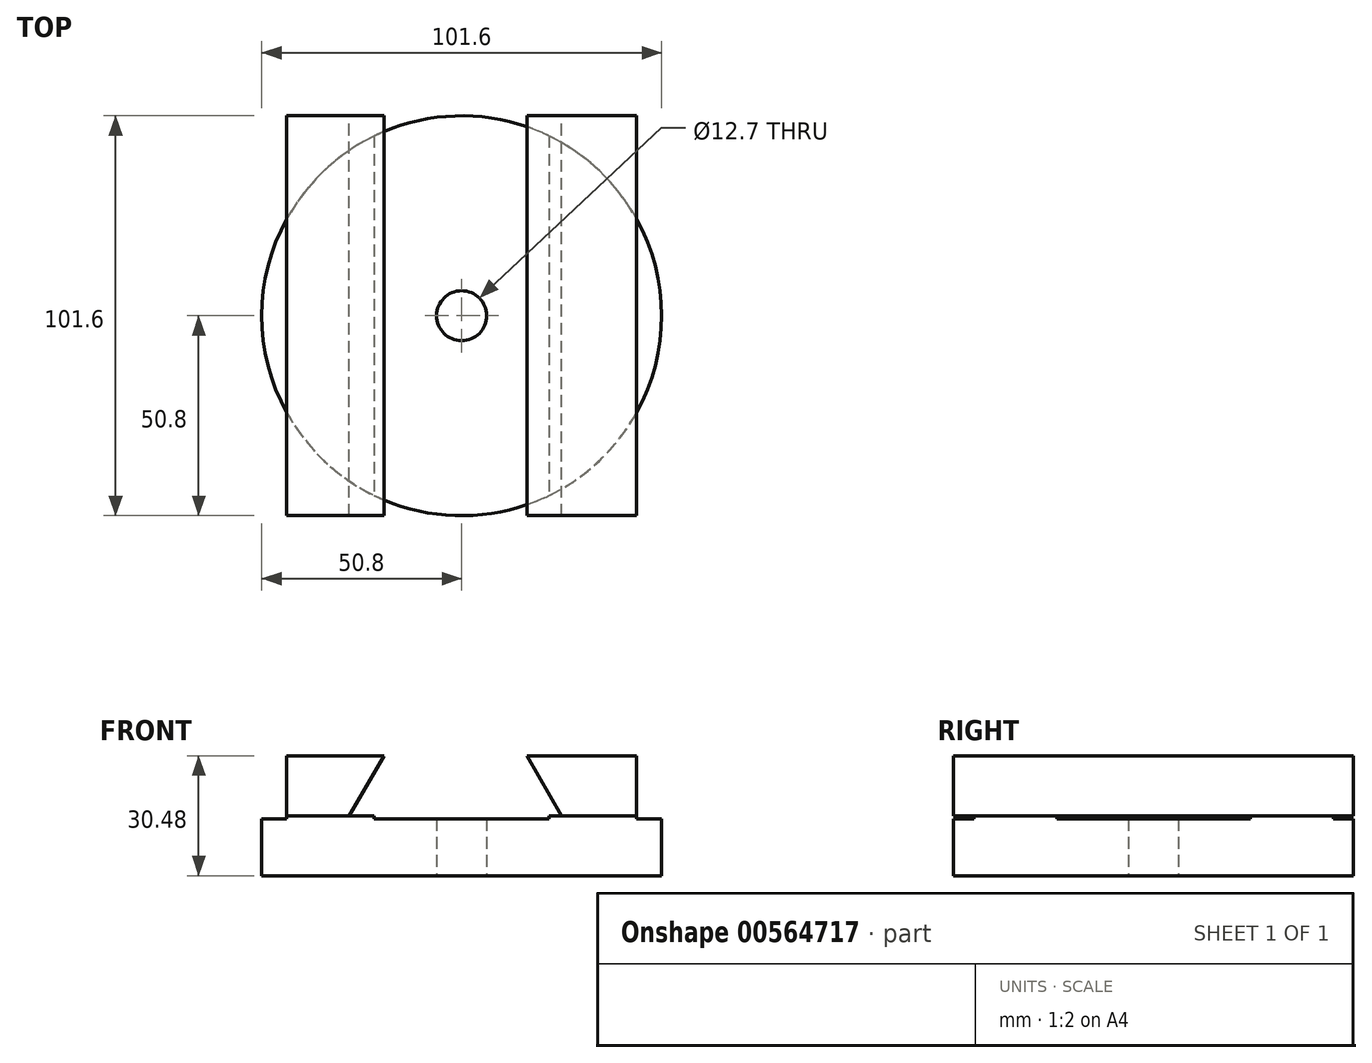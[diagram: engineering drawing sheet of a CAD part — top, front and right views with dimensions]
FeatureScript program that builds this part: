
annotation { "Feature Type Name" : "Feature", "Feature Type Description" : "" }
export const myFeature = defineFeature(function(context is Context, id is Id, definition is map)
    precondition{}
    {
        {
            var Q0;
            Q0=qCreatedBy(makeId("Top.planeOp"),FACE);
            var sketch = newSketch(context, id + "F0", { "sketchPlane" : qUnion([Q0])});
            skCircle(sketch, "E0", {"center": v(0, 0) * mm, "radius": 50.8 * mm});
            skSolve(sketch);
        }
        {
            var Q0;
            Q0=makeQuery(id+"F0.imprint","IMPRINT",FACE,{"disambiguationData":[TD([[makeQuery(id+"F0.imprint","IMPRINT",EDGE,{"derivedFrom":sQuery(id+"F0.wireOp",EDGE,"E0")}),1.0]])]});
            extrude(context, id + "F1", {"entities" : qUnion([Q0]), "depth" : 15.24 * mm, "offsetDistance" : 25.4 * mm});
        }
        {
            var Q0;
            Q0=sQuery(id+"F0.wireOp",VERTEX,"E0.center");
            var Q1;
            Q1=makeQuery(id+"F1.opExtrude","SWEPT_BODY",BODY,{"disambiguationData":[OSD([sQuery(id+"F0.wireOp",EDGE,"E0")])]});
            hole(context, id + "F2", {"style" : HoleStyle.SIMPLE, "endStyle" : HoleEndStyle.THROUGH, "oppositeDirection" : true, "holeDiameter" : 12.7 * mm, "isTappedThrough" : true, "tappedDepth" : 12.7 * mm, "tapClearance" : 3, "locations" : qUnion([Q0]), "scope" : qUnion([Q1])});
        }
        {
            var Q0;
            Q0=makeQuery(id+"F1.opExtrude","CAP_FACE",FACE,{"disambiguationData":[OSD([sQuery(id+"F0.wireOp",EDGE,"E0")])],"isStart":false});
            var sketch = newSketch(context, id + "F3", { "sketchPlane" : qUnion([Q0])});
            skLineSegment(sketch, "E1", {"start": v(-25.4, 44) * mm, "end": v(-25.4, -44) * mm});
            skLineSegment(sketch, "E2", {"start": v(25.4, 44) * mm, "end": v(25.4, -44) * mm});
            skLineSegment(sketch, "E3", {"start": v(0, 50.8) * mm, "end": v(0, -50.8) * mm, "construction": true});
            skLineSegment(sketch, "E4", {"start": v(-44.45, 24.6) * mm, "end": v(-44.45, -24.6) * mm});
            skLineSegment(sketch, "E5", {"start": v(44.45, 24.6) * mm, "end": v(44.45, -24.6) * mm});
            skLineSegment(sketch, "E6", {"start": v(22.23, 45.68) * mm, "end": v(22.23, -45.68) * mm});
            skLineSegment(sketch, "E7", {"start": v(-22.23, 45.68) * mm, "end": v(-22.23, -45.68) * mm});
            skSolve(sketch);
        }
        {
            var Q0;
            {var subQ0=sQuery(id+"F3.wireOp",EDGE,"E4");Q0=makeQuery(id+"F3.imprint","IMPRINT",FACE,{"disambiguationData":[TD([[makeQuery(id+"F3.imprint","IMPRINT",EDGE,{"derivedFrom":subQ0}),-1.0]])]});}
            var Q1;
            {var subQ0=sQuery(id+"F3.wireOp",EDGE,"E5");Q1=makeQuery(id+"F3.imprint","IMPRINT",FACE,{"disambiguationData":[TD([[makeQuery(id+"F3.imprint","IMPRINT",EDGE,{"derivedFrom":subQ0}),1.0]])]});}
            var Q2;
            {var subQ0=sQuery(id+"F3.wireOp",EDGE,"E6");Q2=makeQuery(id+"F3.imprint","IMPRINT",FACE,{"disambiguationData":[TD([[makeQuery(id+"F3.imprint","IMPRINT",EDGE,{"derivedFrom":subQ0}),-1.0]])]});}
            extrude(context, id + "F4", {"entities" : qUnion([Q0, Q1, Q2]), "operationType" : NewBodyOperationType.REMOVE, "oppositeDirection" : true, "depth" : 0.79 * mm, "offsetDistance" : 25.4 * mm});
        }
        {
            var Q0;
            Q0=qCreatedBy(makeId("Front.planeOp"),FACE);
            var sketch = newSketch(context, id + "F5", { "sketchPlane" : qUnion([Q0])});
            skLineSegment(sketch, "E8.0", {"start": v(25.4, 15.24) * mm, "end": v(44.45, 15.24) * mm});
            skLineSegment(sketch, "E9", {"start": v(-44.45, 30.48) * mm, "end": v(-19.78, 30.48) * mm});
            skLineSegment(sketch, "E10", {"start": v(44.45, 15.24) * mm, "end": v(44.45, 30.48) * mm});
            skLineSegment(sketch, "E11", {"start": v(-44.45, 15.24) * mm, "end": v(-44.45, 30.48) * mm});
            skLineSegment(sketch, "E12", {"start": v(25.4, 15.24) * mm, "end": v(16.6, 30.48) * mm});
            skLineSegment(sketch, "E13", {"start": v(16.6, 30.48) * mm, "end": v(44.45, 30.48) * mm});
            skLineSegment(sketch, "E14.0", {"start": v(22.62, 15.24) * mm, "end": v(44.45, 15.24) * mm});
            skLineSegment(sketch, "E15", {"start": v(-44.45, 15.24) * mm, "end": v(-22.23, 15.24) * mm});
            skLineSegment(sketch, "E16", {"start": v(-19.78, 30.48) * mm, "end": v(-28.58, 15.24) * mm});
            skLineSegment(sketch, "E17", {"start": v(-19.78, 30.48) * mm, "end": v(16.6, 30.48) * mm, "construction": true});
            skLineSegment(sketch, "E18", {"start": v(-22.23, 15.24) * mm, "end": v(22.23, 15.24) * mm, "construction": true});
            skLineSegment(sketch, "E19", {"start": v(-44.45, 22.86) * mm, "end": v(44.45, 22.86) * mm, "construction": true});
            skPoint(sketch, "E20", {"position": v(0, 22.86) * mm});
            skCircle(sketch, "E21", {"center": v(0, 22.86) * mm, "radius": 4.76 * mm, "construction": true});
            skLineSegment(sketch, "E22", {"start": v(-7.94, 30.48) * mm, "end": v(-7.94, 15.24) * mm, "construction": true});
            skLineSegment(sketch, "E23", {"start": v(7.94, 30.48) * mm, "end": v(7.94, 15.24) * mm, "construction": true});
            skLineSegment(sketch, "E24", {"start": v(0, 30.48) * mm, "end": v(0, 15.24) * mm, "construction": true});
            skSolve(sketch);
        }
        {
            var Q0;
            {var subQ0=sQuery(id+"F5.wireOp",EDGE,"E10");Q0=makeQuery(id+"F5.imprint","IMPRINT",FACE,{"disambiguationData":[TD([[makeQuery(id+"F5.imprint","IMPRINT",EDGE,{"derivedFrom":subQ0}),1.0]])]});}
            var Q1;
            Q1=makeQuery(id+"F5.imprint","IMPRINT",FACE,{"disambiguationData":[TD([[makeQuery(id+"F5.imprint","IMPRINT",EDGE,{"derivedFrom":sQuery(id+"F5.wireOp",EDGE,"E9")}),-1.0]])]});
            extrude(context, id + "F6", {"entities" : qUnion([Q0, Q1]), "depth" : 50.8 * mm, "offsetDistance" : 25.4 * mm, "hasSecondDirection" : true, "secondDirectionOppositeDirection" : true, "secondDirectionDepth" : 50.8 * mm});
        }
    });
